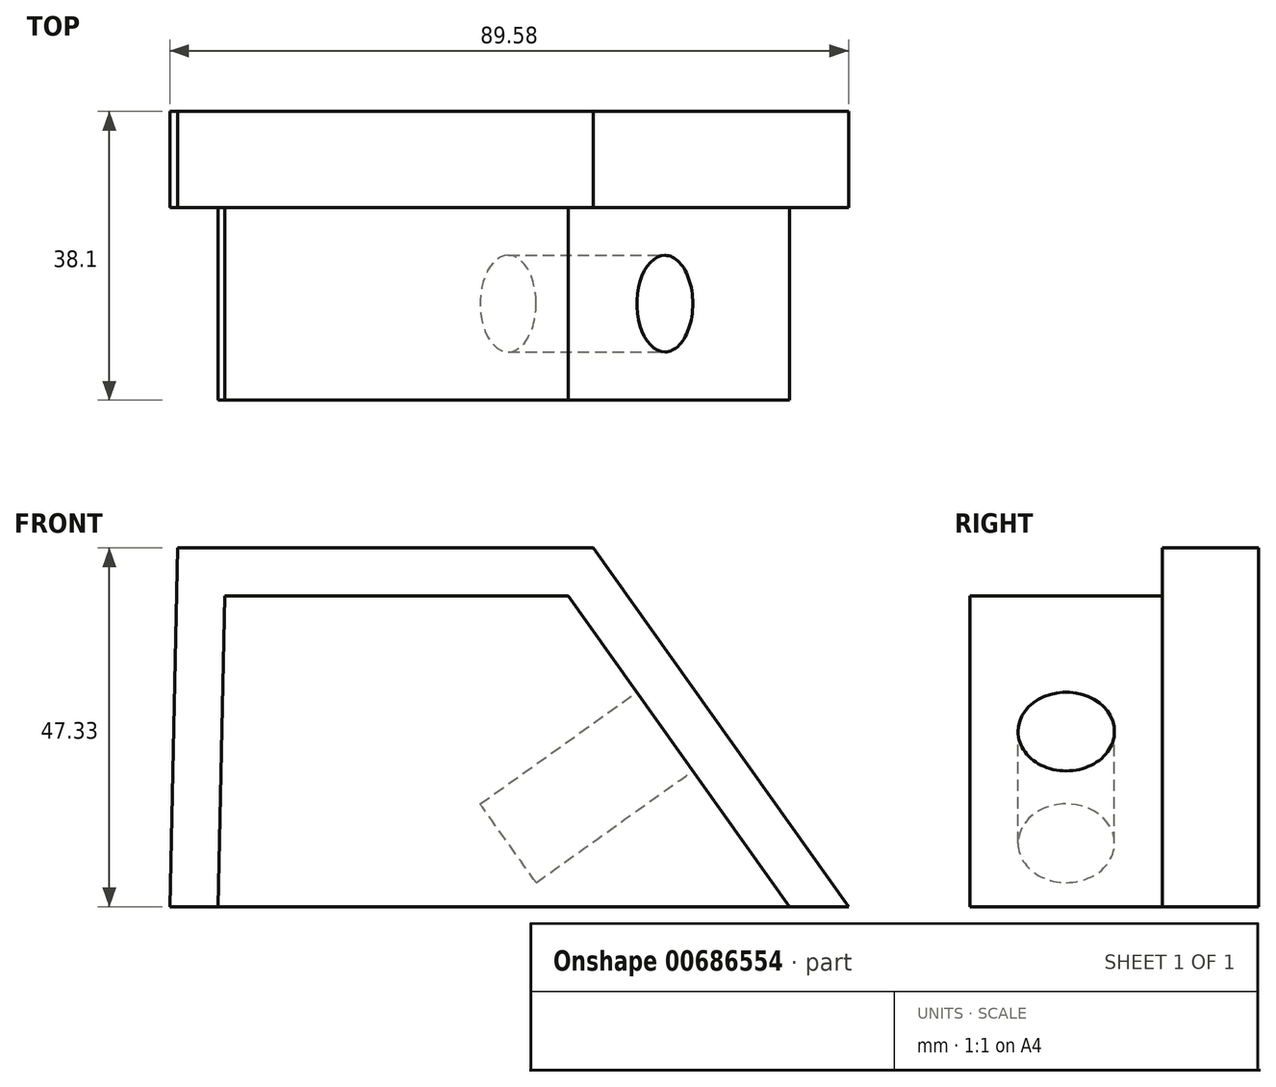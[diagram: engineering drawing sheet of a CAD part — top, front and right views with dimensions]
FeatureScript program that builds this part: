
annotation { "Feature Type Name" : "Feature", "Feature Type Description" : "" }
export const myFeature = defineFeature(function(context is Context, id is Id, definition is map)
    precondition{}
    {
        {
            var Q0;
            Q0=qCreatedBy(makeId("Front.planeOp"),FACE);
            var sketch = newSketch(context, id + "F0", { "sketchPlane" : qUnion([Q0])});
            skLineSegment(sketch, "E0.0", {"start": v(-31.68, 33.92) * mm, "end": v(23.18, 33.92) * mm});
            skLineSegment(sketch, "E0.1", {"start": v(-32.7, -13.4) * mm, "end": v(-31.68, 33.92) * mm});
            skLineSegment(sketch, "E0.2", {"start": v(56.88, -13.4) * mm, "end": v(-32.7, -13.4) * mm});
            skLineSegment(sketch, "E0.3", {"start": v(23.18, 33.92) * mm, "end": v(56.88, -13.4) * mm});
            skSolve(sketch);
        }
        {
            var Q0;
            Q0=makeQuery(id+"F0.imprint","IMPRINT",FACE,{"disambiguationData":[TD([[makeQuery(id+"F0.imprint","IMPRINT",EDGE,{"derivedFrom":sQuery(id+"F0.wireOp",EDGE,"E0.0")}),-1.0]])]});
            extrude(context, id + "F1", {"entities" : qUnion([Q0]), "depth" : 12.7 * mm, "offsetDistance" : 25.4 * mm});
        }
        {
            var Q0;
            Q0=makeQuery(id+"F1.opExtrude","CAP_FACE",FACE,{"disambiguationData":[OSD([sQuery(id+"F0.wireOp",EDGE,"E0.0"),sQuery(id+"F0.wireOp",EDGE,"E0.1"),sQuery(id+"F0.wireOp",EDGE,"E0.2"),sQuery(id+"F0.wireOp",EDGE,"E0.3")])],"isStart":false});
            var sketch = newSketch(context, id + "F2", { "sketchPlane" : qUnion([Q0])});
            skLineSegment(sketch, "E1.0", {"start": v(19.9, 27.57) * mm, "end": v(49.09, -13.4) * mm});
            skLineSegment(sketch, "E1.1", {"start": v(-25.47, 27.57) * mm, "end": v(19.9, 27.57) * mm});
            skLineSegment(sketch, "E1.2", {"start": v(-26.35, -13.54) * mm, "end": v(-25.47, 27.57) * mm});
            skLineSegment(sketch, "E2", {"start": v(-26.35, -13.54) * mm, "end": v(49.09, -13.4) * mm});
            skSolve(sketch);
        }
        {
            var Q0;
            {var subQ0=sQuery(id+"F2.wireOp",EDGE,"E1.0");Q0=makeQuery(id+"F2.imprint","IMPRINT",FACE,{"disambiguationData":[TD([[makeQuery(id+"F2.imprint","IMPRINT",EDGE,{"derivedFrom":subQ0}),-1.0]])]});}
            extrude(context, id + "F3", {"entities" : qUnion([Q0]), "operationType" : NewBodyOperationType.ADD, "depth" : 25.4 * mm, "offsetDistance" : 25.4 * mm});
        }
        {
            var Q0;
            Q0=makeQuery(id+"F3.opExtrude","SWEPT_FACE",FACE,{"disambiguationData":[OSD([sQuery(id+"F2.wireOp",EDGE,"E1.0")])]});
            var sketch = newSketch(context, id + "F4", { "sketchPlane" : qUnion([Q0])});
            skCircle(sketch, "E3", {"center": v(-25.36, -11.04) * mm, "radius": 6.37 * mm});
            skSolve(sketch);
        }
        {
            var Q0;
            Q0=makeQuery(id+"F4.imprint","IMPRINT",FACE,{"disambiguationData":[TD([[makeQuery(id+"F4.imprint","IMPRINT",EDGE,{"derivedFrom":sQuery(id+"F4.wireOp",EDGE,"E3")}),1.0]])]});
            extrude(context, id + "F5", {"entities" : qUnion([Q0]), "operationType" : NewBodyOperationType.REMOVE, "oppositeDirection" : true, "depth" : 25.4 * mm, "offsetDistance" : 25.4 * mm});
        }
    });
